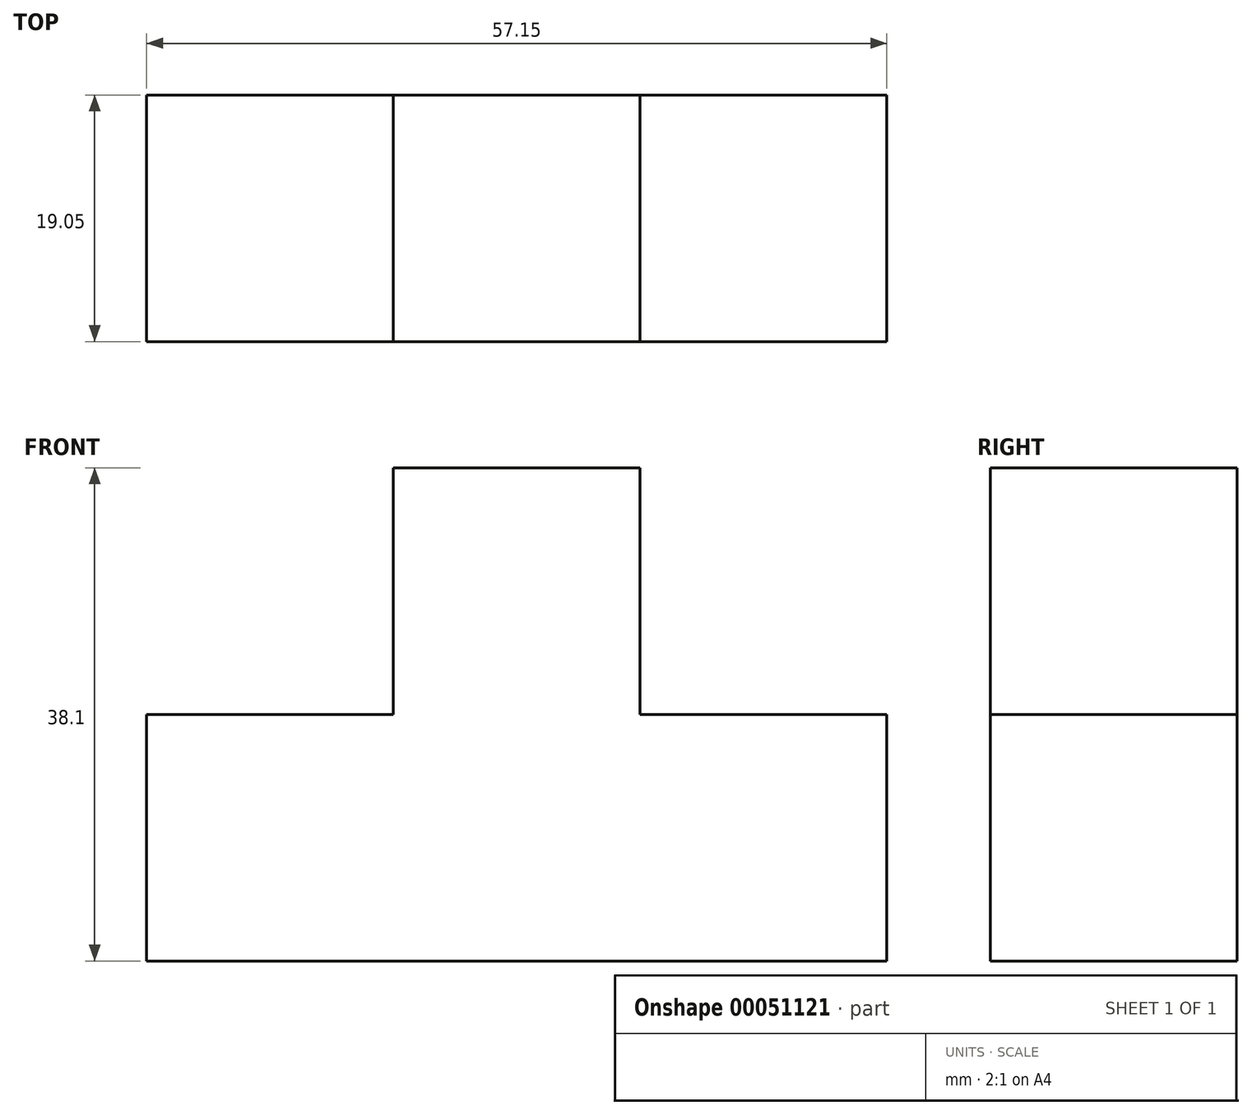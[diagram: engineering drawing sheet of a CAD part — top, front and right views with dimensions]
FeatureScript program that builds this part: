
annotation { "Feature Type Name" : "Feature", "Feature Type Description" : "" }
export const myFeature = defineFeature(function(context is Context, id is Id, definition is map)
    precondition{}
    {
        {
            var Q0;
            Q0=qCreatedBy(makeId("Top.planeOp"),FACE);
            var sketch = newSketch(context, id + "F0", { "sketchPlane" : qUnion([Q0])});
            skLineSegment(sketch, "E0.bottom", {"start": v(-30.17, -4.28) * mm, "end": v(26.98, -4.28) * mm});
            skLineSegment(sketch, "E0.top", {"start": v(-30.17, -23.33) * mm, "end": v(26.98, -23.33) * mm});
            skLineSegment(sketch, "E0.left", {"start": v(-30.17, -4.28) * mm, "end": v(-30.17, -23.33) * mm});
            skLineSegment(sketch, "E0.right", {"start": v(26.98, -4.28) * mm, "end": v(26.98, -23.33) * mm});
            skSolve(sketch);
        }
        {
            var Q0;
            Q0 = qSketchRegion(id + "F0", true);
            extrude(context, id + "F1", {"entities" : qUnion([Q0]), "depth" : 19.05 * mm});
        }
        {
            var Q0;
            Q0=makeQuery(id+"F1.opExtrude","CAP_FACE",FACE,{"disambiguationData":[OSD([sQuery(id+"F0.wireOp",EDGE,"E0.bottom"),sQuery(id+"F0.wireOp",EDGE,"E0.top"),sQuery(id+"F0.wireOp",EDGE,"E0.left"),sQuery(id+"F0.wireOp",EDGE,"E0.right")])],"isStart":false});
            var sketch = newSketch(context, id + "F2", { "sketchPlane" : qUnion([Q0])});
            skLineSegment(sketch, "E1.bottom", {"start": v(-30.17, -4.28) * mm, "end": v(-11.12, -4.28) * mm});
            skLineSegment(sketch, "E1.top", {"start": v(-30.17, -23.33) * mm, "end": v(-11.12, -23.33) * mm});
            skLineSegment(sketch, "E1.left", {"start": v(-30.17, -4.28) * mm, "end": v(-30.17, -23.33) * mm});
            skLineSegment(sketch, "E1.right", {"start": v(-11.12, -4.28) * mm, "end": v(-11.12, -23.33) * mm});
            skLineSegment(sketch, "E2.bottom", {"start": v(-11.12, -23.33) * mm, "end": v(7.93, -23.33) * mm});
            skLineSegment(sketch, "E2.top", {"start": v(-11.12, -4.28) * mm, "end": v(7.93, -4.28) * mm});
            skLineSegment(sketch, "E2.left", {"start": v(-11.12, -23.33) * mm, "end": v(-11.12, -4.28) * mm});
            skLineSegment(sketch, "E2.right", {"start": v(7.93, -23.33) * mm, "end": v(7.93, -4.28) * mm});
            skSolve(sketch);
        }
        {
            var Q0;
            Q0=makeQuery(id+"F2.imprint","IMPRINT",FACE,{"disambiguationData":[TD([[makeQuery(id+"F2.imprint","IMPRINT",EDGE,{"derivedFrom":sQuery(id+"F2.wireOp",EDGE,"E2.bottom")}),1.0]])]});
            extrude(context, id + "F3", {"entities" : qUnion([Q0]), "operationType" : NewBodyOperationType.ADD, "depth" : 19.05 * mm});
        }
    });
